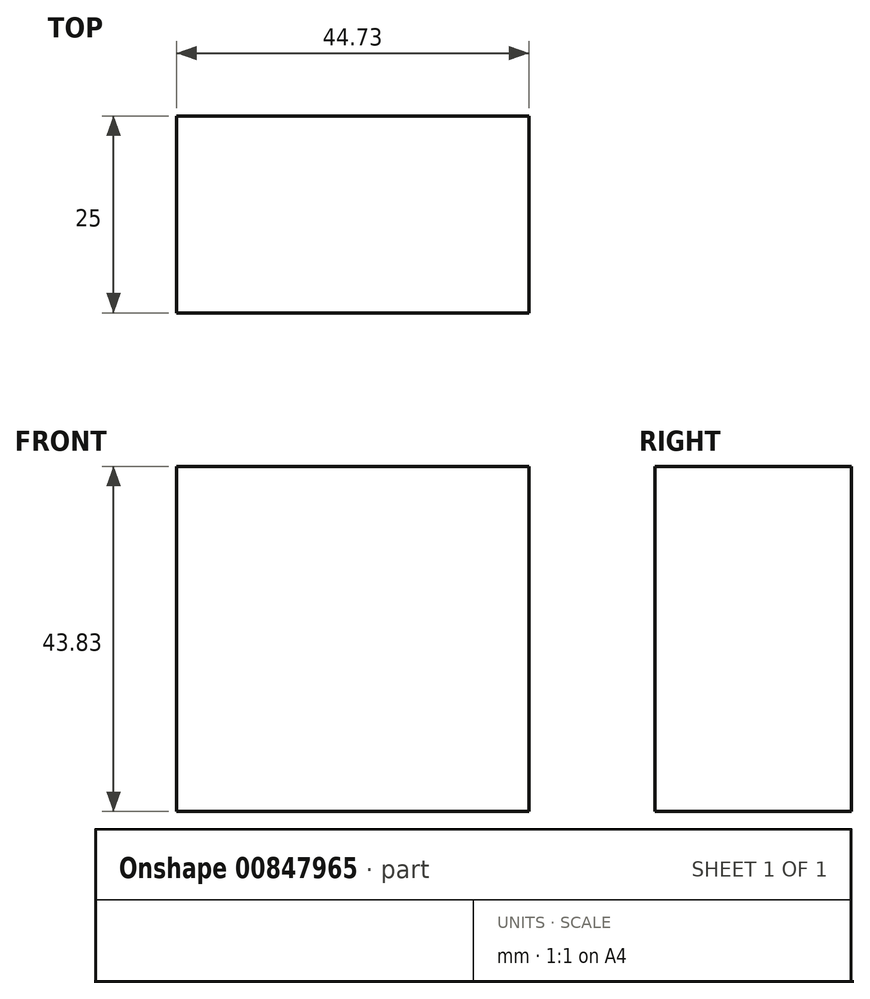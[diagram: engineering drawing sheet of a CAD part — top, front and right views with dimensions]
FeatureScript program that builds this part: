
annotation { "Feature Type Name" : "Feature", "Feature Type Description" : "" }
export const myFeature = defineFeature(function(context is Context, id is Id, definition is map)
    precondition{}
    {
        {
            var Q0;
            Q0=qCreatedBy(makeId("Front.planeOp"),FACE);
            var sketch = newSketch(context, id + "F0", { "sketchPlane" : qUnion([Q0])});
            skLineSegment(sketch, "E0.bottom", {"start": v(-136.19, 26.94) * mm, "end": v(-91.46, 26.94) * mm});
            skLineSegment(sketch, "E0.top", {"start": v(-136.19, -16.89) * mm, "end": v(-91.46, -16.89) * mm});
            skLineSegment(sketch, "E0.left", {"start": v(-136.19, 26.94) * mm, "end": v(-136.19, -16.89) * mm});
            skLineSegment(sketch, "E0.right", {"start": v(-91.46, 26.94) * mm, "end": v(-91.46, -16.89) * mm});
            skSolve(sketch);
        }
        {
            var Q0;
            Q0 = qSketchRegion(id + "F0", true);
            extrude(context, id + "F1", {"entities" : qUnion([Q0]), "depth" : 25 * mm, "offsetDistance" : 25 * mm});
        }
    });
